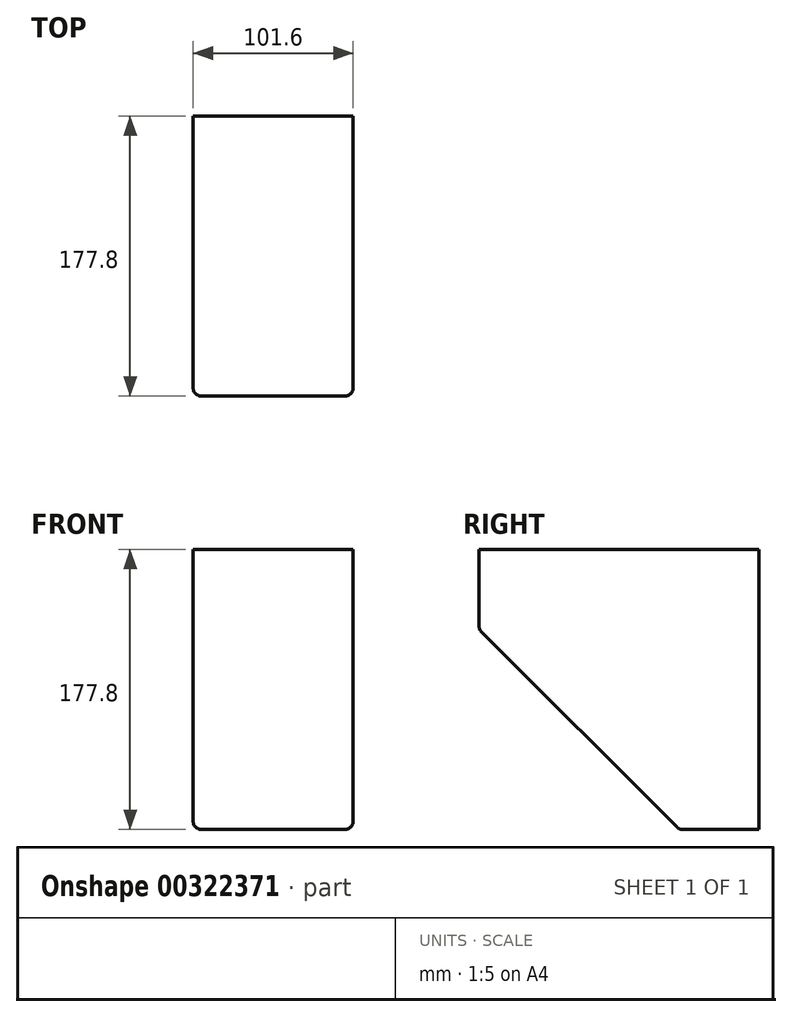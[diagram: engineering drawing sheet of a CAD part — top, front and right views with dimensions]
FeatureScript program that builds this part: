
annotation { "Feature Type Name" : "Feature", "Feature Type Description" : "" }
export const myFeature = defineFeature(function(context is Context, id is Id, definition is map)
    precondition{}
    {
        {
            var Q0;
            Q0=qCreatedBy(makeId("Right.planeOp"),FACE);
            var sketch = newSketch(context, id + "F0", { "sketchPlane" : qUnion([Q0])});
            skLineSegment(sketch, "E0", {"start": v(0, 88.9) * mm, "end": v(-177.8, 88.9) * mm});
            skLineSegment(sketch, "E1", {"start": v(-177.8, 88.9) * mm, "end": v(-177.8, 38.1) * mm});
            skLineSegment(sketch, "E2", {"start": v(-50.8, -88.9) * mm, "end": v(0, -88.9) * mm});
            skLineSegment(sketch, "E3", {"start": v(0, -88.9) * mm, "end": v(0, 88.9) * mm});
            skLineSegment(sketch, "E4", {"start": v(-177.8, 38.1) * mm, "end": v(-50.8, -88.9) * mm});
            skSolve(sketch);
        }
        {
            var Q0;
            Q0=makeQuery(id+"F0.imprint","IMPRINT",FACE,{"disambiguationData":[TD([[makeQuery(id+"F0.imprint","IMPRINT",EDGE,{"derivedFrom":sQuery(id+"F0.wireOp",EDGE,"E0")}),1.0]])]});
            extrude(context, id + "F1", {"entities" : qUnion([Q0]), "endBound" : BoundingType.SYMMETRIC, "depth" : 101.6 * mm});
        }
        {
            var Q0;
            Q0=makeQuery(id+"F1.opExtrude","SWEPT_EDGE",EDGE,{"disambiguationData":[OSD([sQuery(id+"F0.wireOp",EDGE,"E1"),sQuery(id+"F0.wireOp",EDGE,"E4")])]});
            var Q1;
            Q1=makeQuery(id+"F1.opExtrude","SWEPT_EDGE",EDGE,{"disambiguationData":[OSD([sQuery(id+"F0.wireOp",EDGE,"E2"),sQuery(id+"F0.wireOp",EDGE,"E4")])]});
            var Q2;
            Q2=makeQuery(id+"F1.opExtrude","CAP_EDGE",EDGE,{"disambiguationData":[OSD([sQuery(id+"F0.wireOp",EDGE,"E1")])],"isStart":false});
            var Q3;
            Q3=makeQuery(id+"F1.opExtrude","CAP_EDGE",EDGE,{"disambiguationData":[OSD([sQuery(id+"F0.wireOp",EDGE,"E4")])],"isStart":false});
            var Q4;
            Q4=makeQuery(id+"F1.opExtrude","CAP_EDGE",EDGE,{"disambiguationData":[OSD([sQuery(id+"F0.wireOp",EDGE,"E2")])],"isStart":false});
            var Q5;
            Q5=makeQuery(id+"F1.opExtrude","CAP_EDGE",EDGE,{"disambiguationData":[OSD([sQuery(id+"F0.wireOp",EDGE,"E1")])],"isStart":true});
            var Q6;
            Q6=makeQuery(id+"F1.opExtrude","CAP_EDGE",EDGE,{"disambiguationData":[OSD([sQuery(id+"F0.wireOp",EDGE,"E4")])],"isStart":true});
            var Q7;
            Q7=makeQuery(id+"F1.opExtrude","CAP_EDGE",EDGE,{"disambiguationData":[OSD([sQuery(id+"F0.wireOp",EDGE,"E2")])],"isStart":true});
            fillet(context, id + "F2", {"entities" : qUnion([Q0, Q1, Q2, Q3, Q4, Q5, Q6, Q7]), "radius" : 5.08 * mm, "tangentPropagation" : true, "allowEdgeOverflow" : false});
        }
    });
